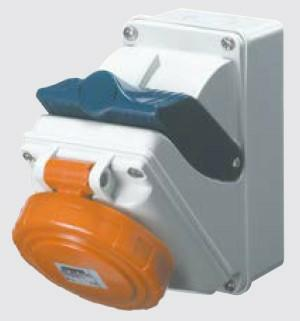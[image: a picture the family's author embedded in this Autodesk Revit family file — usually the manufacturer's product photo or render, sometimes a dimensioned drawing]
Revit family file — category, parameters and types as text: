
# Revit family: Building-ConnessioniIEC309-GEWISS-COMBIBLOC-PRESE-INTERBLOCCATE_IP55
name_source: partatom
category: Apparecchi elettrici
units: mm (PartAtom-declared; Revit-internal decimal feet)

## family parameters
Condiviso = No
Host = Superficie
Mantenere orientamento annotazione = Sì
Punto di calcolo locali = Sì
Quota connettore circolare = Usa diametro
Taglio con vuoti quando caricato = No
Tipo di parte = Normale

## types (18) — shared parameters
BLOCCO = B=C
Catalogo = BUILDING
Codice Electrocod = 2221
Con fondo = Si
FORMULA = 1000 mm  [stored 3.28084 ft]
Frequenza = 50/60 Hz
Glow wire test: = 850 °C (Parti attive) - 650 °C (Parti passive)
Grado di protezione = IP55
IDF = b7f7b9c2-e9bc-4798-b8cf-a7b123c56d69
IDT = 876c997d56934812acb3c8df0937ea93
Immagine tipo = COMBIBLOC55Fondo.jpg
L = 155 mm
N.poli = 1
POMELLO = bianco
PRESA = Giallo
Produttore = GEWISS S.p.A.
Prospetto di default = 1219 mm
Protezione = NO (SBF)
Resistenza agli urti = IK08
SEO = Presa interbloccata
STRUTTURA = RAL - 7035
STRUTTURA ALTA = blue
Scheda Tecnica = https://www.gewiss.com
Spostamento_S = 1500 mm
Temperatura di utilizzo = -25 +40 °C
Termopressione con biglia = 125 °C (Parti attive) - 80 °C (Parti passive)
Tipologia = Compatta
URL = https://www.gewiss.com
VETRO = Vetro
Versione file RFA = 21.4
Voltaggio = 0 V
W = 115 mm

## per-type parameters (varying)
| type | Colore: | Corrente nominale (A) | Descrizione | Modello | N. poli | Riferimento h | Tensione nominale |
| GW66464 - COMBIBLOC C.F.IP55 3P+N+T 32A 400V 6H | Rosso | 32 | COMBIBLOC C.F.IP55 3P+N+T 32A 400V 6H | GW66464 | 3P+N+T | 6 | 380-415V |
| GW66456 - COMBIBLOC C.F.IP55 2P+T 32A 110V 4H | Giallo | 32 | COMBIBLOC C.F.IP55 2P+T 32A 110V 4H | GW66456 | 2P+T | 4 | 100-130V |
| GW66453 - COMBIBLOC C.F.IP55 3P+N+T 16A 400V 6H | Rosso | 16 | COMBIBLOC C.F.IP55 3P+N+T 16A 400V 6H | GW66453 | 3P+N+T | 6 | 380-415V |
| GW66460 - COMBIBLOC C.F.IP55 3P+T 32A 230V 9H | Blu | 32 | COMBIBLOC C.F.IP55 3P+T 32A 230V 9H | GW66460 | 3P+T | 9 | 200-250V |
| GW66448 - COMBIBLOC C.F.IP55 2P+T 16A 230V 6H | Blu | 16 | COMBIBLOC C.F.IP55 2P+T 16A 230V 6H | GW66448 | 2P+T | 6 | 200-250V |
| GW66451 - COMBIBLOC C.F.IP55 2P+T 16A 400V 9H | Rosso | 16 | COMBIBLOC C.F.IP55 2P+T 16A 400V 9H | GW66451 | 2P+T | 9 | 380-415V |
| GW66461 - COMBIBLOC C.F.IP55 3P+N+T 32A 230V 9H | Blu | 32 | COMBIBLOC C.F.IP55 3P+N+T 32A 230V 9H | GW66461 | 3P+N+T | 9 | 200-250V |
| GW66463 - COMBIBLOC C.F.IP55 3P+T 32A 400V 6H | Rosso | 32 | COMBIBLOC C.F.IP55 3P+T 32A 400V 6H | GW66463 | 3P+T | 6 | 380-415V |
| GW66459 - COMBIBLOC C.F.IP55 2P+T 32A 230V 6H | Blu | 32 | COMBIBLOC C.F.IP55 2P+T 32A 230V 6H | GW66459 | 2P+T | 6 | 200-250V |
| GW66449 - COMBIBLOC C.F.IP55 3P+T 16A 230V 9H | Blu | 16 | COMBIBLOC C.F.IP55 3P+T 16A 230V 9H | GW66449 | 3P+T | 9 | 200-250V |
| GW66452 - COMBIBLOC C.F.IP55 3P+T 16A 400V 6H | Rosso | 16 | COMBIBLOC C.F.IP55 3P+T 16A 400V 6H | GW66452 | 3P+T | 6 | 380-415V |
| GW66445 - COMBIBLOC C.F.IP55 2P+T 16A 110V 4H | Giallo | 16 | COMBIBLOC C.F.IP55 2P+T 16A 110V 4H | GW66445 | 2P+T | 4 | 100-130V |
| GW66457 - COMBIBLOC C.F.IP55 3P+T 32A 110V 4H | Giallo | 32 | COMBIBLOC C.F.IP55 3P+T 32A 110V 4H | GW66457 | 3P+T | 4 | 100-130V |
| GW66447 - COMBIBLOC C.F.IP55 3P+N+T 16A 110V 4H | Giallo | 16 | COMBIBLOC C.F.IP55 3P+N+T 16A 110V 4H | GW66447 | 3P+N+T | 4 | 100-130V |
| GW66450 - COMBIBLOC C.F.IP55 3P+N+T 16A 230V 9H | Blu | 16 | COMBIBLOC C.F.IP55 3P+N+T 16A 230V 9H | GW66450 | 3P+N+T | 9 | 200-250V |
| GW66446 - COMBIBLOC C.F.IP55 3P+T 16A 110V 4H | Giallo | 16 | COMBIBLOC C.F.IP55 3P+T 16A 110V 4H | GW66446 | 3P+T | 4 | 100-130V |
| GW66462 - COMBIBLOC C.F.IP55 2P+T 32A 400V 9H | Rosso | 32 | COMBIBLOC C.F.IP55 2P+T 32A 400V 9H | GW66462 | 2P+T | 9 | 380-415V |
| GW66458 - COMBIBLOC C.F.IP55 3P+N+T 32A 110V 4H | Giallo | 32 | COMBIBLOC C.F.IP55 3P+N+T 32A 110V 4H | GW66458 | 3P+N+T | 4 | 100-130V |

note: [stored X ft] marks values corroborated as IEEE doubles in the binary element streams (Revit-internal decimal feet)

## geometry (parser evidence)
native form markers: Sweep x4
no freeform markers — native parametric forms only
